# Revit family: Vandal Proof Batten_Emergency_Ceiling-Hosted_R16_V1.1
name_source: partatom
category: Lighting Fixtures
revit_build: Autodesk Revit 2016 (Build: 20150220_1215(x64)
units: mm (PartAtom-declared; Revit-internal decimal feet)

## family parameters
Always vertical = Yes
Cut with Voids When Loaded = No
Host = Ceiling
Light Source = Yes
OmniClass Number = 23.80.70.11
OmniClass Title = Luminaries for Internal Lighting
Part Type = Normal
Room Calculation Point = No
Round Connector Dimension = Use Diameter
Shared = No
Work Plane-Based = No

## types (3) — shared parameters
AS2293 Classification = C0=D100 C90=D40
Battery Type = Lithium Nonophosphate, 6.6V 2500mAh
Ceiling = <By Category>
Charging Method = Intelligent Current Limited Constant Voltage
Color Filter = 16777215
Construction = Pressure Die-cast, Low Copper AL Alloy Body with Grey P/Coat Base, Removable Gear Tray & Replaceable LED modules, Battery POD at one end
Diffuser = Opal, Impact Resistant Polycarbonate with Secure Access Screws
Dimensions = 1400 x 140 x 120mm (L x W x H) including battery POD
Dimming Lamp Color Temperature Shift = <None>
Driver/Ballast = Tridonic LC 50W 350-1050mA
Emit Shape Visible in Rendering = No
Emit from Rectangle Length = 1219 mm
Emit from Rectangle Width = 610 mm
IK Rating = IK10
IP Rating = IP66
Lamp = 2 x LED module, 4000K natural white, 50,000h [L80/B20, Ta40C], Ra>80
Mounting = Surface Mount
Operating Mode = Maintained
Operating Temperature = 0C to 40C
Operating Voltage = 240V AC; 50Mz
Photometric Web File = 6035_LVP4LEDM-P-ZW_80mA_EM_ProductionDiffuser_18082017-02.ies
Power Consumption = 44W (lamps ON, 0.4W (lamps OFF)
Tilt Angle = 90.00°

## per-type parameters (varying)
| type | Product Description | Testing Mode |
| LVP4LEDM-P | L10 Optimum 4ft Argonaut LED Vandal Batten with Battery POD and LED Module/Light Engines, Enabled with Clevertest Plus | Clevertest Plus Enabled (not activated by default) |
| LVP4LEDM-P-ZW | L10 Optimum 4ft Argonaut LED Vandal Batten with Battery POD and LED Module/Light Engines | Zoneworks Computer Testing |
| LVP4LEDM-P-DALI | L10 Optimum 4ft Argonaut LED Vandal Batten with Battery POD and LED Module/Light Engines | DALI Compatible |

## geometry (parser evidence)
native form markers: Sweep x3
no freeform markers — native parametric forms only
